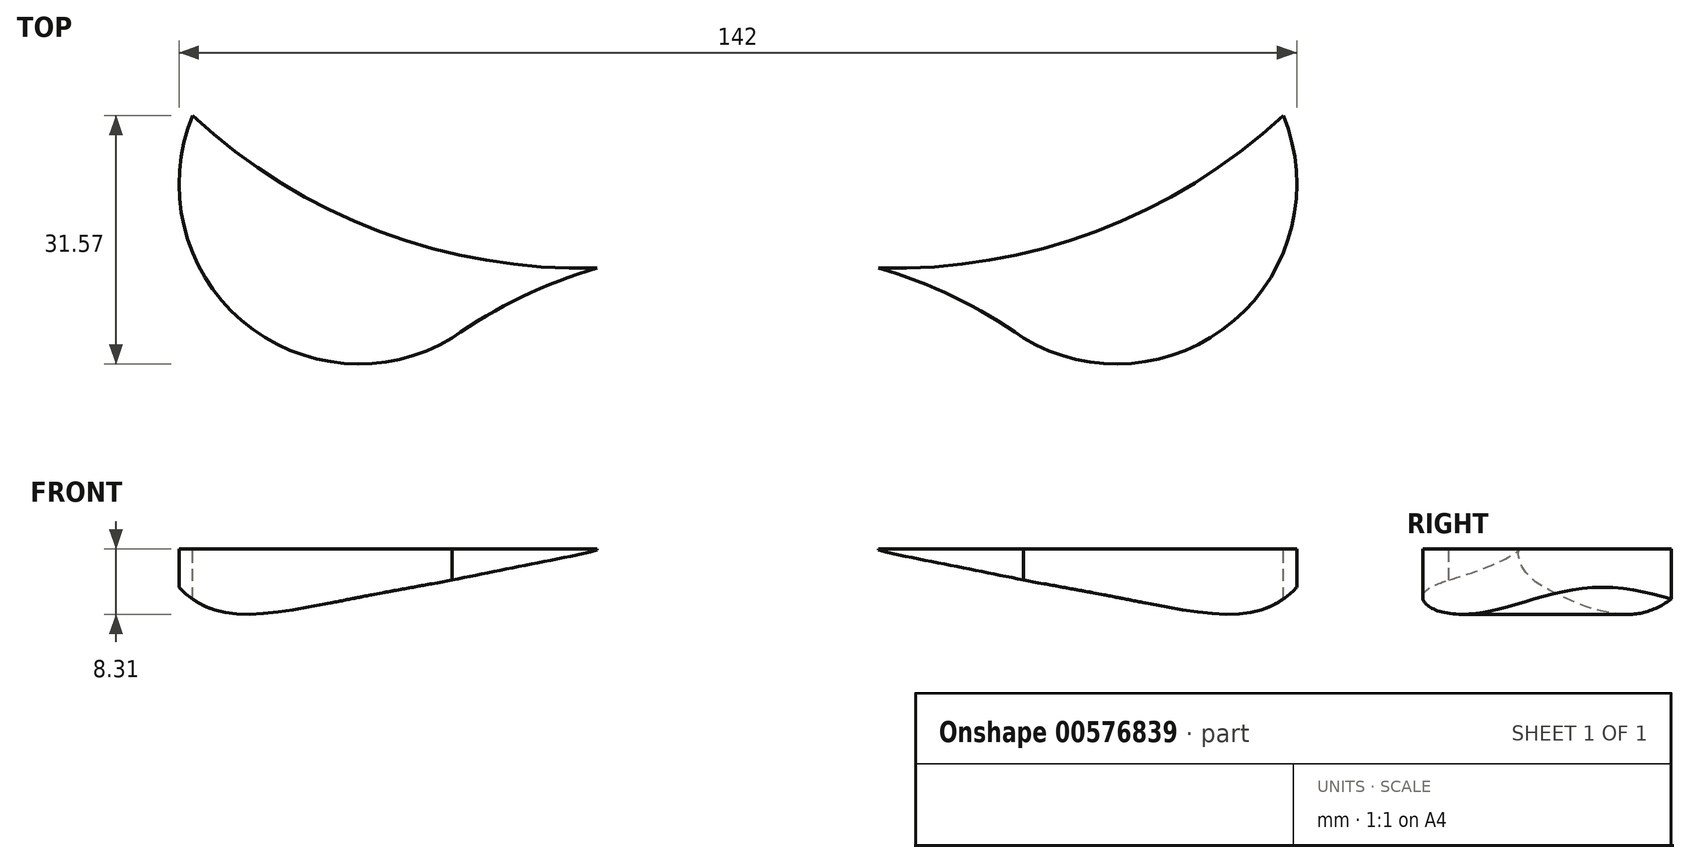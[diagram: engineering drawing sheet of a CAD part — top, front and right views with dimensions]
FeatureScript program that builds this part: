
annotation { "Feature Type Name" : "Feature", "Feature Type Description" : "" }
export const myFeature = defineFeature(function(context is Context, id is Id, definition is map)
    precondition{}
    {
        {
            var Q0;
            Q0=qCreatedBy(makeId("Top.planeOp"),FACE);
            var sketch = newSketch(context, id + "F0", { "sketchPlane" : qUnion([Q0])});
            skArc(sketch, "E0", {"start": v(36.28, 50.32) * mm, "mid": v(63, 52.5) * mm, "end": v(69.27, 78.57) * mm});
            skArc(sketch, "E1", {"start": v(35.45, -52.63) * mm, "mid": v(66.08, -57.97) * mm, "end": v(83.81, -32.44) * mm});
            skLineSegment(sketch, "E2", {"start": v(83.81, -32.44) * mm, "end": v(83.81, -6.7) * mm});
            skArc(sketch, "E3", {"start": v(54.95, -31.3) * mm, "mid": v(64.63, -28.54) * mm, "end": v(71.98, -21.65) * mm});
            skLineSegment(sketch, "E4", {"start": v(71.98, -21.65) * mm, "end": v(83.81, -6.7) * mm});
            skArc(sketch, "E5", {"start": v(17.88, 59.2) * mm, "mid": v(45.48, 63.83) * mm, "end": v(69.27, 78.57) * mm});
            skLineSegment(sketch, "E6", {"start": v(17.32, -61.1) * mm, "end": v(20.44, -80.48) * mm});
            skArc(sketch, "E7", {"start": v(-20.44, -80.48) * mm, "mid": v(0, -117.87) * mm, "end": v(20.44, -80.48) * mm});
            skLineSegment(sketch, "E8.MirrorCS", {"start": v(-17.32, -61.1) * mm, "end": v(-20.44, -80.48) * mm});
            skArc(sketch, "E9.MirrorCS", {"start": v(60.32, -18.46) * mm, "mid": v(-17.32, -61.1) * mm, "end": v(-59.87, 16.6) * mm});
            skArc(sketch, "E10.MirrorCS", {"start": v(60.32, -18.46) * mm, "mid": v(17.77, 59.23) * mm, "end": v(-59.87, 16.6) * mm});
            skLineSegment(sketch, "E11.MirrorCS", {"start": v(-71.98, -21.65) * mm, "end": v(-83.81, -6.7) * mm});
            skArc(sketch, "E12.MirrorCS", {"start": v(-54.95, -31.3) * mm, "mid": v(-64.63, -28.54) * mm, "end": v(-71.98, -21.65) * mm});
            skLineSegment(sketch, "E13.MirrorCS", {"start": v(-83.81, -32.44) * mm, "end": v(-83.81, -6.7) * mm});
            skArc(sketch, "E14.MirrorCS", {"start": v(-35.45, -52.63) * mm, "mid": v(-66.08, -57.97) * mm, "end": v(-83.81, -32.44) * mm});
            skArc(sketch, "E15.MirrorCS", {"start": v(-60.32, -18.46) * mm, "mid": v(-17.77, 59.23) * mm, "end": v(59.87, 16.6) * mm});
            skArc(sketch, "E16.MirrorCS", {"start": v(-60.32, -18.46) * mm, "mid": v(17.32, -61.1) * mm, "end": v(59.87, 16.6) * mm});
            skArc(sketch, "E17.MirrorCS", {"start": v(-17.88, 59.2) * mm, "mid": v(-45.48, 63.83) * mm, "end": v(-69.27, 78.57) * mm});
            skArc(sketch, "E18.MirrorCS", {"start": v(-36.28, 50.32) * mm, "mid": v(-63, 52.5) * mm, "end": v(-69.27, 78.57) * mm});
            skLineSegment(sketch, "E19", {"start": v(0, -63.6) * mm, "end": v(0, 61.73) * mm});
            skLineSegment(sketch, "E20", {"start": v(8.9, 61.06) * mm, "end": v(0, 83.3) * mm});
            skLineSegment(sketch, "E21.MirrorCS", {"start": v(-8.9, 61.06) * mm, "end": v(0, 83.3) * mm});
            skSolve(sketch);
        }
        {
            var Q0;
            {var subQ2=sQuery(id+"F0.wireOp",EDGE,"E19");Q0=makeQuery(id+"F0.imprint","IMPRINT",FACE,{"disambiguationData":[TD([[makeQuery(id+"F0.imprint","IMPRINT",EDGE,{"derivedFrom":subQ2}),-1.0]])]});}
            var Q1;
            Q1=sQuery(id+"F0.wireOp",EDGE,"E19");
            revolve(context, id + "F1", {"entities" : qUnion([Q0]), "axis" : qUnion([Q1]), "revolveType" : RevolveType.ONE_DIRECTION, "angle" : 180 * degree});
        }
        {
            var Q0;
            Q0=qCreatedBy(makeId("Right.planeOp"),FACE);
            var sketch = newSketch(context, id + "F2", { "sketchPlane" : qUnion([Q0])});
            skFitSpline(sketch, "E22", {"points": [v(-57.7, -3.58) * mm, v(-61.35, -5.8) * mm, v(-65.76, -6.35) * mm, v(-72.97, -7.9) * mm, v(-79.66, -9.5) * mm, v(-85.35, -11.21) * mm, v(-89.77, -12.98) * mm, v(-95, -14.96) * mm, v(-99.58, -16.49) * mm, v(-104.32, -17.18) * mm, v(-108.91, -17.23) * mm, v(-113.44, -15.74) * mm, v(-116.27, -13.28) * mm, v(-117.8, -10.16) * mm, v(-118.5, -5.3) * mm, v(-117.5, 0) * mm, v(-117.35, 0) * mm], "startDerivative": vector(-42.76, -42.35) * mm, "endDerivative": vector(12.82, -6.41) * mm});
            skLineSegment(sketch, "E23", {"start": v(-57.7, -3.58) * mm, "end": v(-57.7, 0) * mm});
            skLineSegment(sketch, "E24", {"start": v(-57.7, 0) * mm, "end": v(-117.35, 0) * mm});
            skSolve(sketch);
        }
        {
            var Q0;
            {var subQ6=sQuery(id+"F0.wireOp",EDGE,"E7");Q0=makeQuery(id+"F0.imprint","IMPRINT",FACE,{"disambiguationData":[TD([[makeQuery(id+"F0.imprint","IMPRINT",EDGE,{"derivedFrom":subQ6}),1.0]])]});}
            extrude(context, id + "F3", {"entities" : qUnion([Q0]), "oppositeDirection" : true, "depth" : 17.78 * mm, "offsetDistance" : 25.4 * mm, "hasDraft" : true, "draftAngle" : 6 * degree});
        }
        {
            var Q0;
            Q0 = qSketchRegion(id + "F2", true);
            var Q1;
            Q1=makeQuery(id+"F3.opExtrude","CAP_FACE",FACE,{"disambiguationData":[OSD([sQuery(id+"F0.wireOp",EDGE,"E6"),sQuery(id+"F0.wireOp",EDGE,"E7"),sQuery(id+"F0.wireOp",EDGE,"E8.MirrorCS"),sQuery(id+"F0.wireOp",EDGE,"E9.MirrorCS"),sQuery(id+"F0.wireOp",EDGE,"E16.MirrorCS")])],"isStart":false});
            var Q2;
            Q2=makeQuery(id+"F3.opExtrude","SWEPT_BODY",BODY,{"disambiguationData":[OSD([sQuery(id+"F0.wireOp",EDGE,"E6"),sQuery(id+"F0.wireOp",EDGE,"E7"),sQuery(id+"F0.wireOp",EDGE,"E8.MirrorCS"),sQuery(id+"F0.wireOp",EDGE,"E9.MirrorCS"),sQuery(id+"F0.wireOp",EDGE,"E16.MirrorCS")])]});
            extrude(context, id + "F4", {"entities" : qUnion([Q0]), "operationType" : NewBodyOperationType.INTERSECT, "endBound" : BoundingType.SYMMETRIC, "oppositeDirection" : true, "depth" : 55.37 * mm, "endBoundEntityFace" : qUnion([Q1]), "endBoundEntityBody" : qUnion([Q2]), "offsetDistance" : 25.4 * mm});
        }
        {
            var Q0;
            Q0=qCreatedBy(makeId("Right.planeOp"),FACE);
            var sketch = newSketch(context, id + "F5", { "sketchPlane" : qUnion([Q0])});
            skLineSegment(sketch, "E25", {"start": v(83.37, 0) * mm, "end": v(57.13, -7.1) * mm});
            skLineSegment(sketch, "E26", {"start": v(57.13, -7.1) * mm, "end": v(57.13, 0) * mm});
            skLineSegment(sketch, "E27", {"start": v(57.13, 0) * mm, "end": v(83.37, 0) * mm});
            skSolve(sketch);
        }
        {
            var Q0;
            {var subQ3=sQuery(id+"F0.wireOp",EDGE,"E20");var subQ5=sQuery(id+"F0.wireOp",EDGE,"E21.MirrorCS");var subQ6=makeQuery(id+"F0.imprint","INTERSECT",VERTEX,{"derivedFrom":[subQ3,subQ5]});Q0=makeQuery(id+"F0.imprint","IMPRINT",FACE,{"disambiguationData":[TD([[makeQuery(id+"F0.imprint","IMPRINT",EDGE,{"disambiguationData":[TD([[subQ6,1.0]])],"derivedFrom":subQ3}),1.0]])]});}
            extrude(context, id + "F6", {"entities" : qUnion([Q0]), "oppositeDirection" : true, "depth" : 25.4 * mm, "offsetDistance" : 25.4 * mm});
        }
        {
            var Q0;
            Q0 = qSketchRegion(id + "F5", true);
            var Q1;
            Q1=sQuery(id+"F5.wireOp",EDGE,"E25");
            extrude(context, id + "F7", {"entities" : qUnion([Q0]), "operationType" : NewBodyOperationType.INTERSECT, "surfaceEntities" : qUnion([Q1]), "endBound" : BoundingType.SYMMETRIC, "depth" : 25.9 * mm, "offsetDistance" : 25.4 * mm});
        }
        {
            var Q0;
            Q0=qCreatedBy(makeId("Front.planeOp"),FACE);
            var sketch = newSketch(context, id + "F8", { "sketchPlane" : qUnion([Q0])});
            skFitSpline(sketch, "E28", {"points": [v(30.34, 0) * mm, v(44.66, -2.56) * mm, v(55.6, -4.56) * mm, v(63.28, -6.31) * mm, v(68.96, -8.1) * mm, v(75.18, -8.9) * mm, v(79.99, -7.84) * mm, v(82.72, -5.04) * mm, v(83.85, -2.14) * mm, v(83.95, 0) * mm, v(83.95, 0) * mm, v(30.34, 0) * mm]});
            skSolve(sketch);
        }
        {
            var Q0;
            {var subQ4=sQuery(id+"F0.wireOp",EDGE,"E2");Q0=makeQuery(id+"F0.imprint","IMPRINT",FACE,{"disambiguationData":[TD([[makeQuery(id+"F0.imprint","IMPRINT",EDGE,{"derivedFrom":subQ4}),1.0]])]});}
            extrude(context, id + "F9", {"entities" : qUnion([Q0]), "oppositeDirection" : true, "depth" : 25.4 * mm, "offsetDistance" : 25.4 * mm, "hasDraft" : true, "draftAngle" : 20 * degree});
        }
        {
            var Q0;
            Q0 = qSketchRegion(id + "F8", true);
            extrude(context, id + "F10", {"entities" : qUnion([Q0]), "operationType" : NewBodyOperationType.INTERSECT, "endBound" : BoundingType.SYMMETRIC, "depth" : 132.08 * mm, "offsetDistance" : 25.4 * mm});
        }
        {
            var Q0;
            Q0=qCreatedBy(makeId("Front.planeOp"),FACE);
            var sketch = newSketch(context, id + "F11", { "sketchPlane" : qUnion([Q0])});
            skLineSegment(sketch, "E29", {"start": v(17.88, 0) * mm, "end": v(72.13, 0) * mm});
            skFitSpline(sketch, "E30", {"points": [v(72.13, 0) * mm, v(70.34, -5.52) * mm, v(65.32, -8.05) * mm, v(57.46, -7.87) * mm, v(50.63, -6.63) * mm, v(43.56, -5.27) * mm, v(36.26, -3.93) * mm, v(27.93, -2.24) * mm, v(17.77, 0) * mm, v(17.88, 0) * mm], "startDerivative": vector(9.57, -83.65) * mm, "endDerivative": vector(-27.6, -3.74) * mm});
            skSolve(sketch);
        }
        {
            var Q0;
            {var subQ0=sQuery(id+"F0.wireOp",EDGE,"E0");Q0=makeQuery(id+"F0.imprint","IMPRINT",FACE,{"disambiguationData":[TD([[makeQuery(id+"F0.imprint","IMPRINT",EDGE,{"derivedFrom":subQ0}),1.0]])]});}
            extrude(context, id + "F12", {"entities" : qUnion([Q0]), "oppositeDirection" : true, "depth" : 25.4 * mm, "offsetDistance" : 25.4 * mm});
        }
        {
            var Q0;
            Q0 = qSketchRegion(id + "F11", true);
            extrude(context, id + "F13", {"entities" : qUnion([Q0]), "operationType" : NewBodyOperationType.INTERSECT, "oppositeDirection" : true, "depth" : 101.6 * mm, "offsetDistance" : 25.4 * mm});
        }
        {
            var Q0;
            Q0=makeQuery(id+"F9.opExtrude","SWEPT_BODY",BODY,{"disambiguationData":[OSD([sQuery(id+"F0.wireOp",EDGE,"E1"),sQuery(id+"F0.wireOp",EDGE,"E2"),sQuery(id+"F0.wireOp",EDGE,"E3"),sQuery(id+"F0.wireOp",EDGE,"E4"),sQuery(id+"F0.wireOp",EDGE,"E9.MirrorCS")])]});
            var Q1;
            Q1=makeQuery(id+"F12.opExtrude","SWEPT_BODY",BODY,{"disambiguationData":[OSD([sQuery(id+"F0.wireOp",EDGE,"E0"),sQuery(id+"F0.wireOp",EDGE,"E5"),sQuery(id+"F0.wireOp",EDGE,"E10.MirrorCS")])]});
            var Q2;
            Q2=qCreatedBy(makeId("Right.planeOp"),FACE);
            mirror(context, id + "F14", {"operationType" : NewBodyOperationType.ADD, "entities" : qUnion([Q0, Q1]), "mirrorPlane" : qUnion([Q2])});
        }
    });
